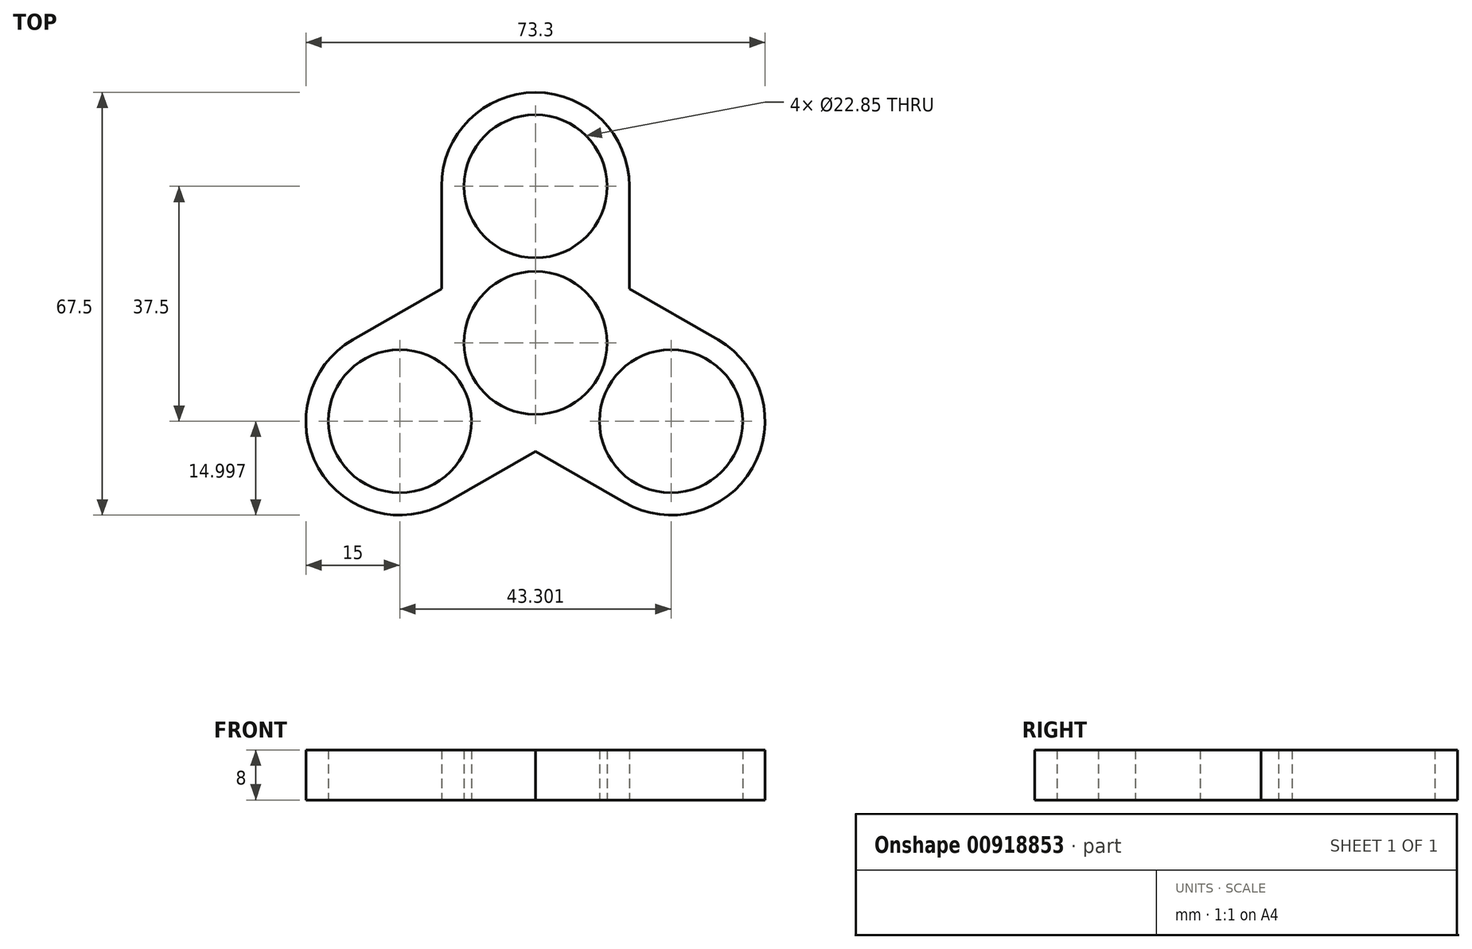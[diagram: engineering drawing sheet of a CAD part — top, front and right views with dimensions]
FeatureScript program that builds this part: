
annotation { "Feature Type Name" : "Feature", "Feature Type Description" : "" }
export const myFeature = defineFeature(function(context is Context, id is Id, definition is map)
    precondition{}
    {
        {
            var Q0;
            Q0=qCreatedBy(makeId("Top.planeOp"),FACE);
            var sketch = newSketch(context, id + "F0", { "sketchPlane" : qUnion([Q0])});
            skCircle(sketch, "E0", {"center": v(-46, 13.18) * mm, "radius": 11.43 * mm});
            skCircle(sketch, "E1", {"center": v(-46, -11.82) * mm, "radius": 11.43 * mm});
            skArc(sketch, "E2", {"start": v(-31, 13.18) * mm, "mid": v(-46, 28.18) * mm, "end": v(-61, 13.18) * mm});
            skArc(sketch, "E3", {"start": v(-61, -11.82) * mm, "mid": v(-46, -26.82) * mm, "end": v(-31, -11.82) * mm});
            skLineSegment(sketch, "E4", {"start": v(-61, 13.18) * mm, "end": v(-61, -11.82) * mm});
            skLineSegment(sketch, "E5", {"start": v(-31, 13.18) * mm, "end": v(-31, -11.82) * mm});
            skLineSegment(sketch, "E6.1.0", {"start": v(-60.16, -37.31) * mm, "end": v(-38.5, -24.81) * mm});
            skArc(sketch, "E6.1.1", {"start": v(-38.5, -24.81) * mm, "mid": v(-33.02, -4.32) * mm, "end": v(-53.5, 1.17) * mm});
            skCircle(sketch, "E6.1.2", {"center": v(-67.66, -24.32) * mm, "radius": 11.43 * mm});
            skLineSegment(sketch, "E6.1.3", {"start": v(-75.16, -11.33) * mm, "end": v(-53.5, 1.17) * mm});
            skArc(sketch, "E6.1.4", {"start": v(-75.16, -11.33) * mm, "mid": v(-80.65, -31.82) * mm, "end": v(-60.16, -37.31) * mm});
            skLineSegment(sketch, "E6.2.0", {"start": v(-16.86, -11.33) * mm, "end": v(-38.5, 1.17) * mm});
            skArc(sketch, "E6.2.1", {"start": v(-38.5, 1.17) * mm, "mid": v(-59, -4.32) * mm, "end": v(-53.5, -24.81) * mm});
            skCircle(sketch, "E6.2.2", {"center": v(-24.36, -24.32) * mm, "radius": 11.43 * mm});
            skLineSegment(sketch, "E6.2.3", {"start": v(-31.86, -37.31) * mm, "end": v(-53.5, -24.81) * mm});
            skArc(sketch, "E6.2.4", {"start": v(-31.86, -37.31) * mm, "mid": v(-11.37, -31.82) * mm, "end": v(-16.86, -11.33) * mm});
            skSolve(sketch);
        }
        {
            var Q0;
            Q0 = qSketchRegion(id + "F0", true);
            var Q1;
            {var subQ9=sQuery(id+"F0.wireOp",EDGE,"E3");Q1=makeQuery(id+"F0.imprint","IMPRINT",FACE,{"disambiguationData":[TD([[makeQuery(id+"F0.imprint","IMPRINT",EDGE,{"derivedFrom":subQ9}),1.0]])]});}
            extrude(context, id + "F1", {"entities" : qUnion([Q0, Q1]), "depth" : 8 * mm, "offsetDistance" : 25 * mm});
        }
    });
